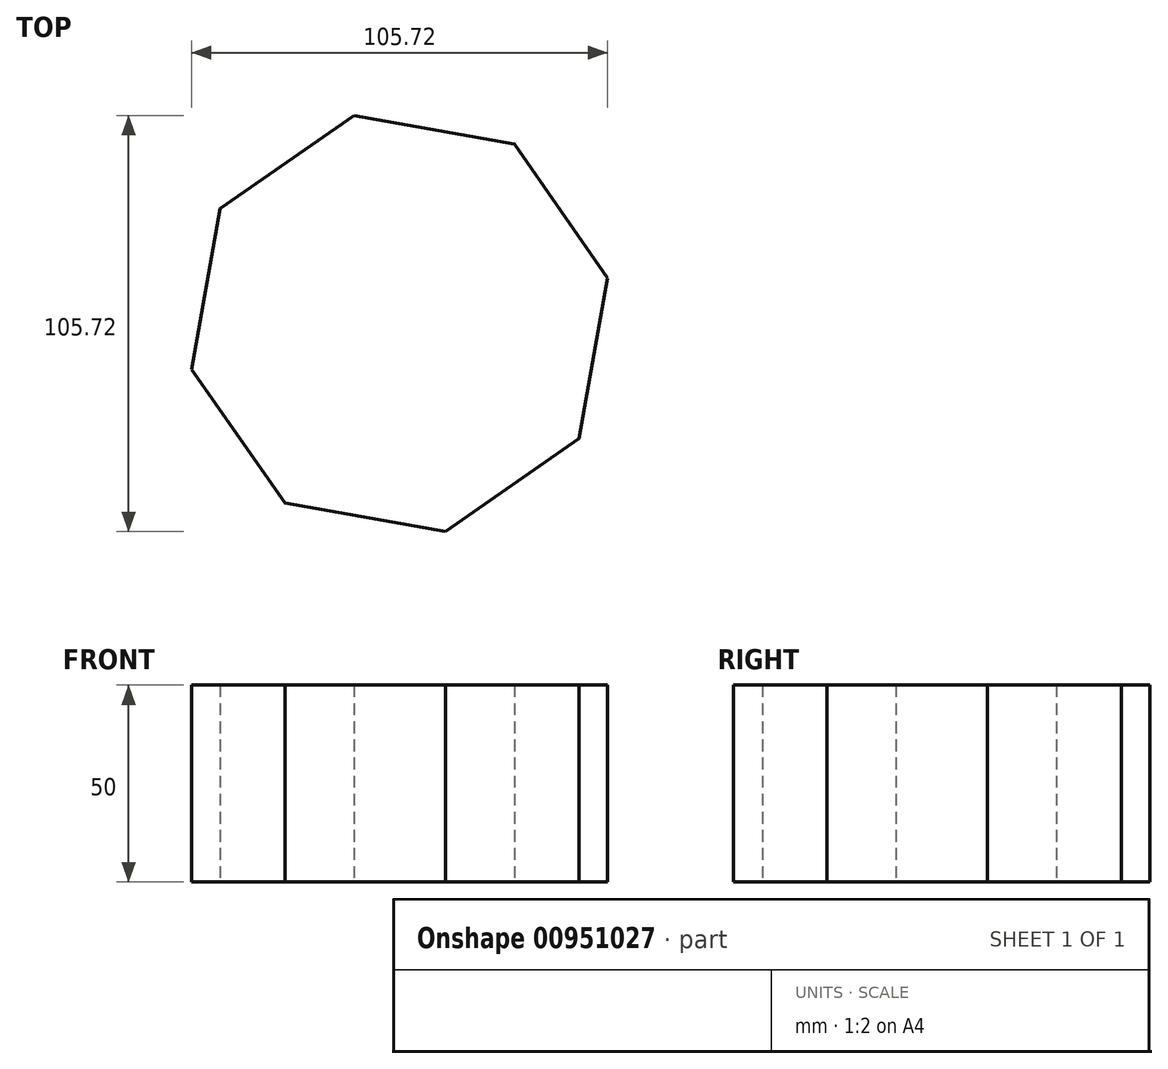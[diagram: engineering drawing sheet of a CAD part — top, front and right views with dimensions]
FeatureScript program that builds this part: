
annotation { "Feature Type Name" : "Feature", "Feature Type Description" : "" }
export const myFeature = defineFeature(function(context is Context, id is Id, definition is map)
    precondition{}
    {
        {
            var Q0;
            Q0=qCreatedBy(makeId("Top.planeOp"),FACE);
            var sketch = newSketch(context, id + "F0", { "sketchPlane" : qUnion([Q0])});
            skCircle(sketch, "E0.cCircle", {"center": v(0, 0) * mm, "radius": 50 * mm, "construction": true});
            skLineSegment(sketch, "E0.0", {"start": v(-45.59, 29.17) * mm, "end": v(-11.6, 52.86) * mm});
            skLineSegment(sketch, "E0.1", {"start": v(-11.6, 52.86) * mm, "end": v(29.17, 45.59) * mm});
            skLineSegment(sketch, "E0.2", {"start": v(29.17, 45.59) * mm, "end": v(52.86, 11.6) * mm});
            skLineSegment(sketch, "E0.3", {"start": v(52.86, 11.6) * mm, "end": v(45.59, -29.17) * mm});
            skLineSegment(sketch, "E0.4", {"start": v(45.59, -29.17) * mm, "end": v(11.6, -52.86) * mm});
            skLineSegment(sketch, "E0.5", {"start": v(11.6, -52.86) * mm, "end": v(-29.17, -45.59) * mm});
            skLineSegment(sketch, "E0.6", {"start": v(-29.17, -45.59) * mm, "end": v(-52.86, -11.6) * mm});
            skLineSegment(sketch, "E0.7", {"start": v(-52.86, -11.6) * mm, "end": v(-45.59, 29.17) * mm});
            skPoint(sketch, "E0.0.midPoint", {"position": v(-28.6, 41.01) * mm});
            skSolve(sketch);
        }
        {
            var Q0;
            Q0 = qSketchRegion(id + "F0", true);
            extrude(context, id + "F1", {"entities" : qUnion([Q0]), "depth" : 50 * mm, "offsetDistance" : 25.4 * mm});
        }
    });
